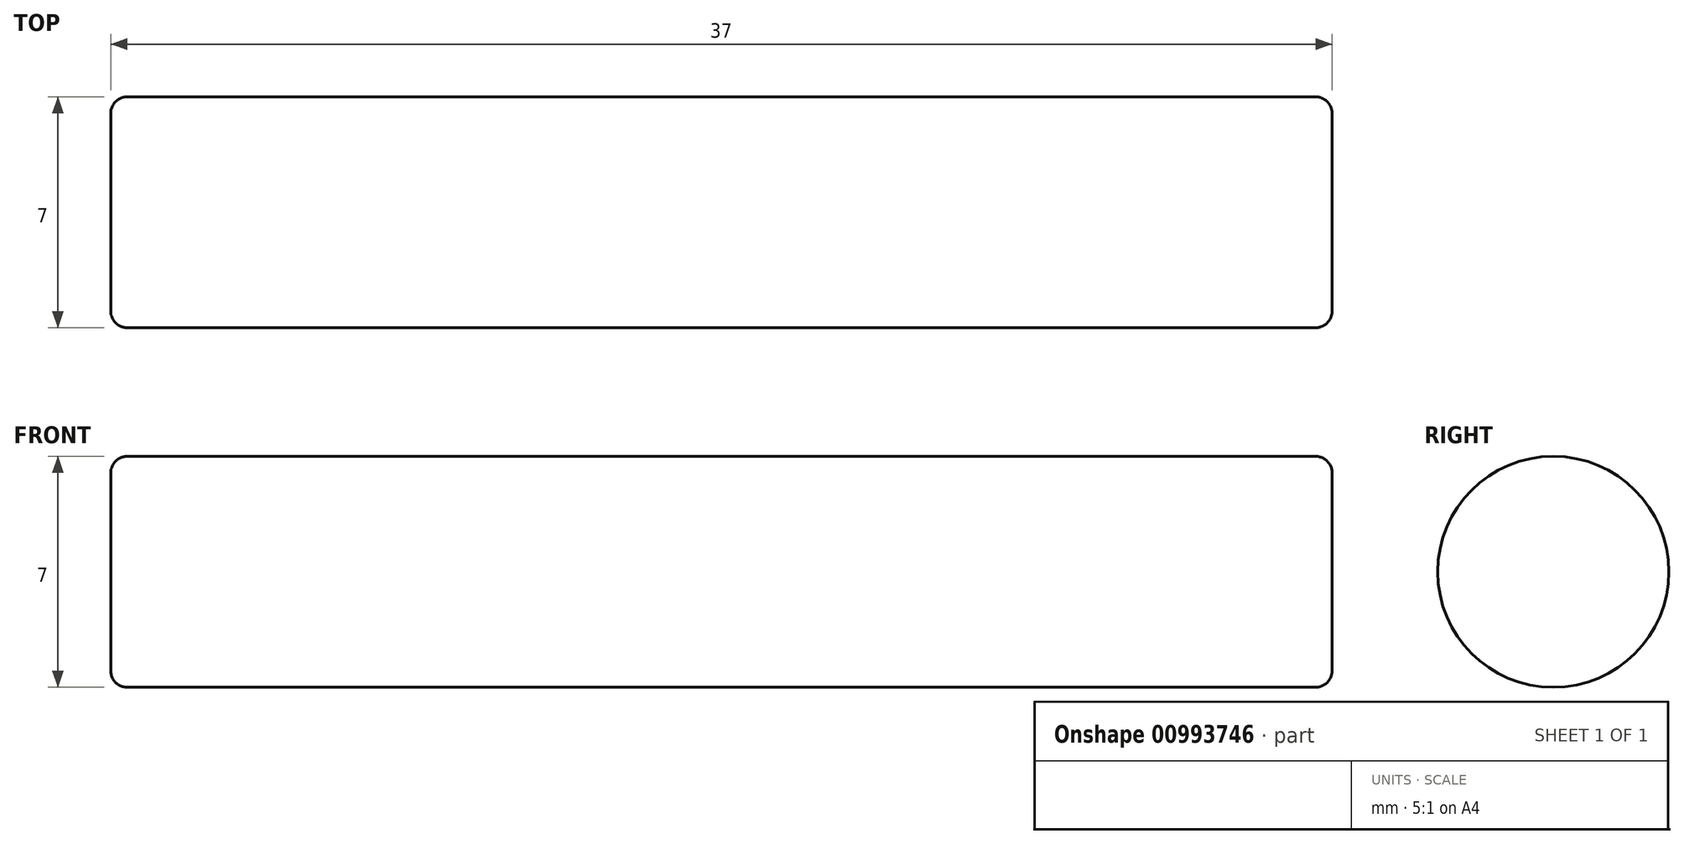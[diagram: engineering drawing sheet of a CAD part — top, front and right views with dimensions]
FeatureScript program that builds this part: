
annotation { "Feature Type Name" : "Feature", "Feature Type Description" : "" }
export const myFeature = defineFeature(function(context is Context, id is Id, definition is map)
    precondition{}
    {
        {
            var Q0;
            Q0=qCreatedBy(makeId("Front.planeOp"),FACE);
            var sketch = newSketch(context, id + "F0", { "sketchPlane" : qUnion([Q0])});
            skLineSegment(sketch, "E0", {"start": v(17, 0) * mm, "end": v(-20, 0) * mm});
            skLineSegment(sketch, "E1", {"start": v(-20, 0) * mm, "end": v(-20, 3.5) * mm});
            skLineSegment(sketch, "E2", {"start": v(-20, 3.5) * mm, "end": v(17, 3.5) * mm});
            skLineSegment(sketch, "E3", {"start": v(17, 3.5) * mm, "end": v(17, 0) * mm});
            skLineSegment(sketch, "E4", {"start": v(15, 3.5) * mm, "end": v(15, 0) * mm});
            skSolve(sketch);
        }
        {
            var Q0;
            {var subQ0=sQuery(id+"F0.wireOp",EDGE,"E1");Q0=makeQuery(id+"F0.imprint","IMPRINT",FACE,{"disambiguationData":[TD([[makeQuery(id+"F0.imprint","IMPRINT",EDGE,{"derivedFrom":subQ0}),-1.0]])]});}
            var Q1;
            {var subQ0=sQuery(id+"F0.wireOp",EDGE,"E3");Q1=makeQuery(id+"F0.imprint","IMPRINT",FACE,{"disambiguationData":[TD([[makeQuery(id+"F0.imprint","IMPRINT",EDGE,{"derivedFrom":subQ0}),-1.0]])]});}
            var Q2;
            Q2=sQuery(id+"F0.wireOp",EDGE,"E0");
            revolve(context, id + "F1", {"surfaceOperationType" : NewSurfaceOperationType.NEW, "entities" : qUnion([Q0, Q1]), "axis" : qUnion([Q2]), "revolveType" : RevolveType.FULL});
        }
        {
            var Q0;
            Q0=makeQuery(id+"F1.opRevolve","SWEPT_EDGE",EDGE,{"disambiguationData":[OSD([sQuery(id+"F0.wireOp",EDGE,"E1"),sQuery(id+"F0.wireOp",EDGE,"E2")])]});
            var Q1;
            Q1=makeQuery(id+"F1.opRevolve","SWEPT_EDGE",EDGE,{"disambiguationData":[OSD([sQuery(id+"F0.wireOp",EDGE,"E2"),sQuery(id+"F0.wireOp",EDGE,"E3")])]});
            fillet(context, id + "F2", {"entities" : qUnion([Q0, Q1]), "radius" : 0.5 * mm, "tangentPropagation" : true, "allowEdgeOverflow" : false});
        }
    });
